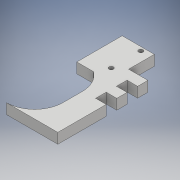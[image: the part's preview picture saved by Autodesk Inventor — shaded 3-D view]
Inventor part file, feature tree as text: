
AUTODESK INVENTOR PART (.ipt)
format: ipt  version: 2017 (Build 210142000, 142)  size: 141,312 bytes
history: native  units: mm
features: sketch x2, extrude x1, hole x1
ambient origin geometry x8: Origin, YZ Plane, XZ Plane, XY Plane, X Axis, Y Axis, Z Axis, Center Point
bodies: Body1 (feature_tree)
feature tree (4):
  extrude  "Extrusion2"  TaperAngle=90.0deg  [1 undecoded]
  hole  "Hole2"  [1 undecoded]
  sketch  "Sketch1"  dims[d0=22.0mm d1=90.0deg]
  sketch  "Sketch5"  dims[d2=0.0mm d3=15.0mm d4=0.0mm d5=13.0mm d6=22.0mm d7=0.0mm d9=15.0mm d14=8.2mm d15=8.2mm d17=7.5mm d32=8.0mm d34=0.0mm d35=8.0mm d37=25.0mm d39=40.0mm d40=0.0mm d41=0.0mm d42=20.0mm d43=8.2mm d44=90.0mm d45=8.0mm d46=0.0mm d47=23.0mm d48=3.0mm d49=0.0mm d50=7.5mm d51=3.4mm d52=6.0mm d53=4.0mm d54=2.0mm d55=90.0deg d56=8.0mm d57=20.594885mm]
note: 2 required parameter values undecoded (feature->parameter linkage not recoverable at this tier; creation-order binding heuristic only, values carry confidence <= 0.55)
